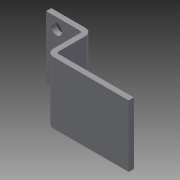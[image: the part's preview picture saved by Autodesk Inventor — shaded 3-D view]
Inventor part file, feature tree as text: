
AUTODESK INVENTOR PART (.ipt)
format: ipt  version: 2013 (Build 170138000, 138)  size: 133,120 bytes
history: native  units: in
note: dims shown in document units (in); Inventor stores cm internally (conversion verified against a paired STEP export)
features: sheet_metal_op x7, sketch x5, other x5, reference x4
ambient origin geometry x8: Origin, YZ Plane, XZ Plane, XY Plane, X Axis, Y Axis, Z Axis, Center Point
bodies: Solid1 (feature_tree)
feature tree (21):
  sheet_metal_op  "Face1"
  sheet_metal_op  "Flange1"
  sheet_metal_op  "Flange2"
  sketch  "Sketch1"  dims[d0=1.5in]
  other  "Plate1"
  sketch  "Sketch2"  dims[d1=0.75in]
  other  "Plate2"
  sheet_metal_op  "Bend1"
  sheet_metal_op  "Corner1"
  sketch  "Sketch3"  dims[d2=0.266in]
  other  "Plate3"
  sheet_metal_op  "Bend2"
  sheet_metal_op  "Corner2"
  sketch  "Sketch4"  dims[d3=0.266in]
  reference  "Reference1"
  sketch  "Sketch5"  dims[d4=1.0in d5=0.25in d6=0.25in d7=0.25in d8=0.125in d9=0.125in d10=0.0625in d11=0.25in d12=0.125in d13=2.0in d14=90.0deg d15=0.05in d16=0.5in d17=0.125in d18=0.125in d19=0.125in d20=0.0625in d21=0.25in d22=0.125in d23=2.25in d24=90.0deg d25=0.05in d26=0.5in d27=0.125in d28=0.125in d29=0.5in d31=0.125in d32=0.0in d33=0.125in d34=0.0in]
  reference  "Reference2"
  reference  "Reference3"
  reference  "Reference4"
  other  "Cut1"
  other  "Cut2"
